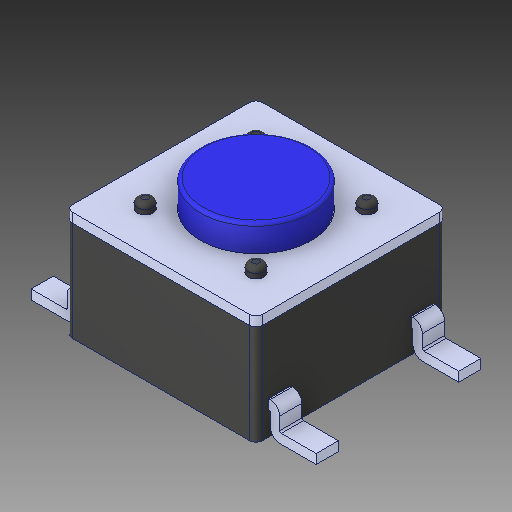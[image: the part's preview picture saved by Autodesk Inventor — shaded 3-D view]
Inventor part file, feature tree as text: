
AUTODESK INVENTOR PART (.ipt)
format: ipt  version: 2018 (Build 220112000, 112)  size: 233,984 bytes
history: native  units: in
note: dims shown in document units (in); Inventor stores cm internally (conversion verified against a paired STEP export)
features: fillet x2, pattern_circular x1, mirror x1
ambient origin geometry x8: Origin, YZ Plane, XZ Plane, XY Plane, X Axis, Y Axis, Z Axis, Center Point
bodies: Solid1 (feature_tree), Solid2 (feature_tree), Solid3 (feature_tree), Solid4 (feature_tree)
feature tree (4):
  fillet  "Fillet6"  [1 undecoded]
  fillet  "Fillet7"  [1 undecoded]
  pattern_circular  "CirPattern3"
  mirror  "Mirror1"
note: 2 required parameter values undecoded (feature->parameter linkage not recoverable at this tier; creation-order binding heuristic only, values carry confidence <= 0.55)
